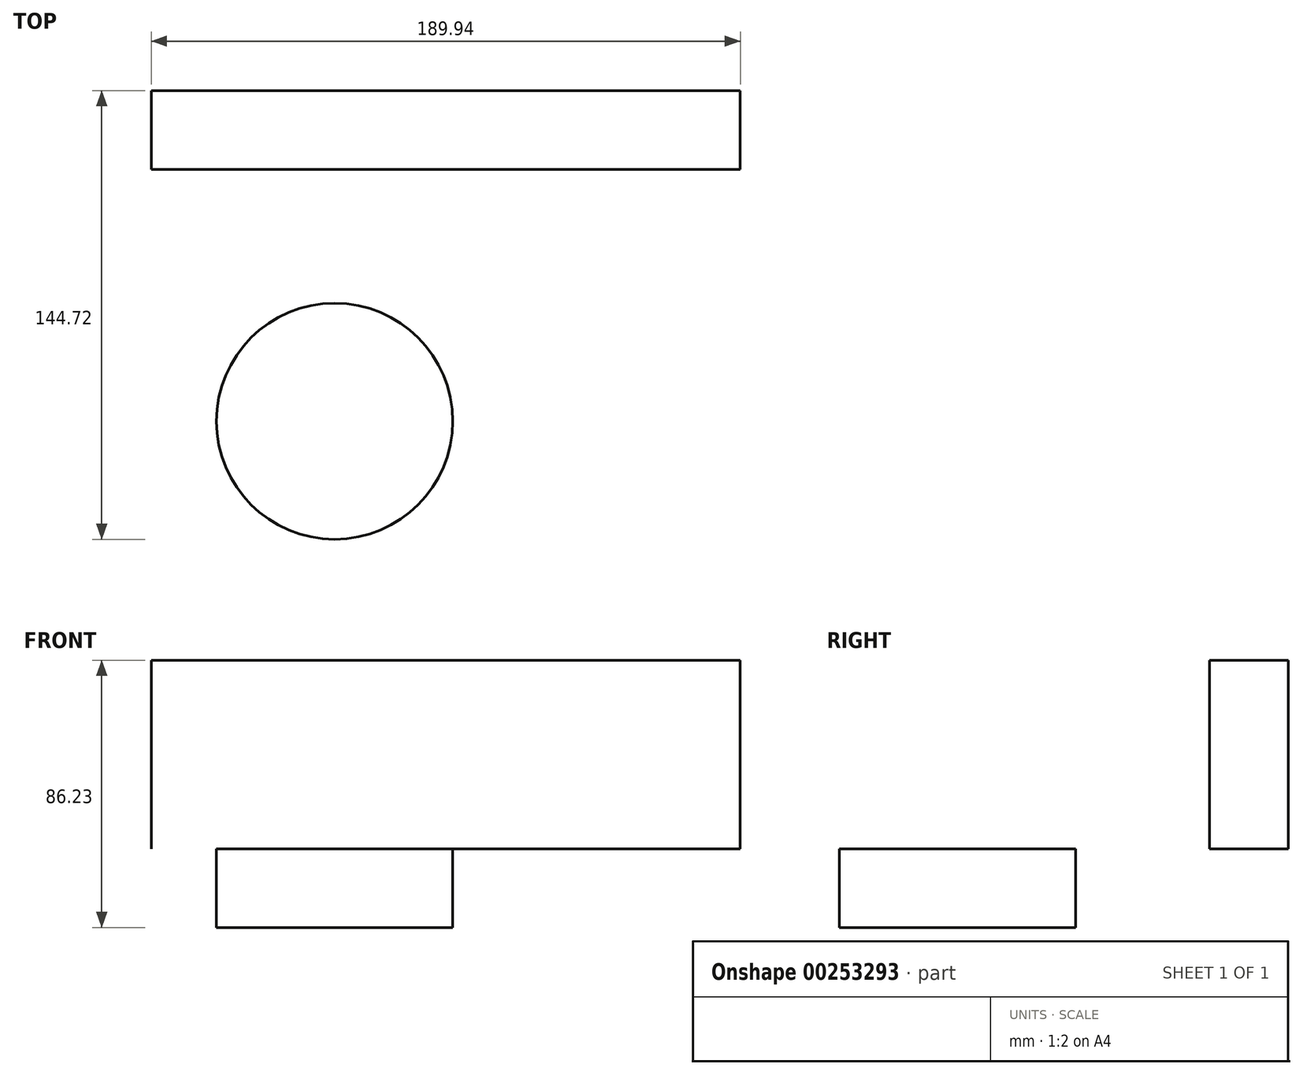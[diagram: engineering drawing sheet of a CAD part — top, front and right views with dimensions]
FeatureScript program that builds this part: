
annotation { "Feature Type Name" : "Feature", "Feature Type Description" : "" }
export const myFeature = defineFeature(function(context is Context, id is Id, definition is map)
    precondition{}
    {
        {
            var Q0;
            Q0=qCreatedBy(makeId("Front.planeOp"),FACE);
            var sketch = newSketch(context, id + "F0", { "sketchPlane" : qUnion([Q0])});
            skLineSegment(sketch, "E0.bottom", {"start": v(25.56, 0) * mm, "end": v(-164.38, 0) * mm});
            skLineSegment(sketch, "E0.top", {"start": v(25.56, 60.83) * mm, "end": v(-164.38, 60.83) * mm});
            skLineSegment(sketch, "E0.left", {"start": v(25.56, 0) * mm, "end": v(25.56, 60.83) * mm});
            skLineSegment(sketch, "E0.right", {"start": v(-164.38, 0) * mm, "end": v(-164.38, 60.83) * mm});
            skPoint(sketch, "E0.middle", {"position": v(-69.41, 30.41) * mm});
            skSolve(sketch);
        }
        {
            var Q0;
            Q0 = qSketchRegion(id + "F0", true);
            extrude(context, id + "F1", {"entities" : qUnion([Q0]), "depth" : 25.4 * mm});
        }
        {
            var Q0;
            Q0=makeQuery(id+"F1.opExtrude","SWEPT_FACE",FACE,{"disambiguationData":[OSD([sQuery(id+"F0.wireOp",EDGE,"E0.bottom")])]});
            var sketch = newSketch(context, id + "F2", { "sketchPlane" : qUnion([Q0])});
            skFitSpline(sketch, "E1", {"points": [v(-298.62, -42.1) * mm, v(-240.74, 35) * mm, v(-195.25, -46.11) * mm, v(-168.77, 19.57) * mm, v(-99.65, -65.93) * mm, v(-60.84, -55.8) * mm], "startDerivative": vector(269.34, 619.67) * mm, "endDerivative": vector(259.32, 218.96) * mm});
            skSolve(sketch);
        }
        {
            var Q0;
            Q0=sQuery(id+"F2.wireOp",EDGE,"E1");
            extrude(context, id + "F3", {"bodyType" : ToolBodyType.SURFACE, "surfaceEntities" : qUnion([Q0]), "depth" : 25.4 * mm});
        }
        {
            var Q0;
            Q0=makeQuery(id+"F1.opExtrude","SWEPT_FACE",FACE,{"disambiguationData":[OSD([sQuery(id+"F0.wireOp",EDGE,"E0.bottom")])]});
            var sketch = newSketch(context, id + "F4", { "sketchPlane" : qUnion([Q0])});
            skEllipse(sketch, "E2", {"center": v(-105.27, 106.62) * mm, "majorRadius": 38.1 * mm, "minorRadius": 38.1 * mm, "majorAxis": v(1, 0)});
            skSolve(sketch);
        }
        {
            var Q0;
            Q0=makeQuery(id+"F4.imprint","IMPRINT",FACE,{"disambiguationData":[TD([[makeQuery(id+"F4.imprint","IMPRINT",EDGE,{"derivedFrom":sQuery(id+"F4.wireOp",EDGE,"E2")}),1.0]])]});
            extrude(context, id + "F5", {"entities" : qUnion([Q0]), "depth" : 25.4 * mm});
        }
    });
